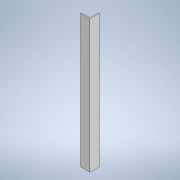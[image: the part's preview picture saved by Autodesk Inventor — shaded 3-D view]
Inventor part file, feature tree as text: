
AUTODESK INVENTOR PART (.ipt)
format: ipt  version: 2022 (Build 260153000, 153)  size: 98,304 bytes
history: native  units: mm
features: extrude x1, sketch x1
ambient origin geometry x8: Origin, YZ Plane, XZ Plane, XY Plane, X Axis, Y Axis, Z Axis, Center Point
bodies: Solid1 (feature_tree)
feature tree (2):
  extrude  "Extrusion1"  Depth=50.0mm
  sketch  "Sketch1"  dims[d0=50.0mm d1=50.0mm d2=5.0mm d3=5.0mm d4=700.0mm d5=0.0mm d6=0.5mm d7=0.872665mm d8=0.5mm d9=0.872665mm]
